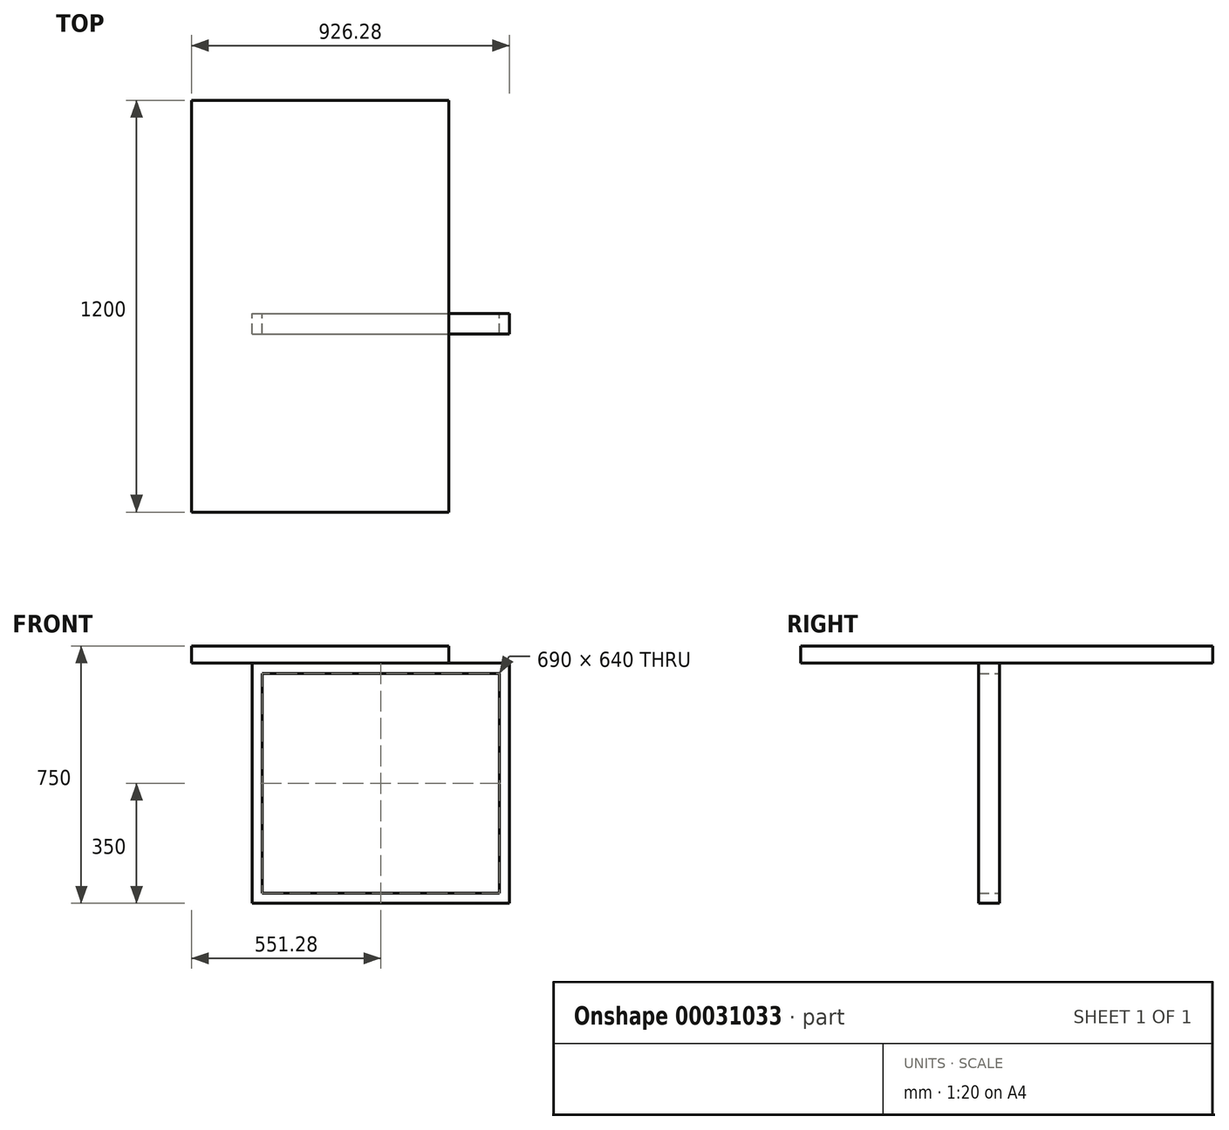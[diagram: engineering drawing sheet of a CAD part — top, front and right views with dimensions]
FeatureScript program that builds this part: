
annotation { "Feature Type Name" : "Feature", "Feature Type Description" : "" }
export const myFeature = defineFeature(function(context is Context, id is Id, definition is map)
    precondition{}
    {
        {
            var Q0;
            Q0=qCreatedBy(makeId("Front.planeOp"),FACE);
            var sketch = newSketch(context, id + "F0", { "sketchPlane" : qUnion([Q0])});
            skLineSegment(sketch, "E0.top", {"start": v(-375, -700) * mm, "end": v(375, -700) * mm});
            skLineSegment(sketch, "E0.left", {"start": v(-375, 0) * mm, "end": v(-375, -700) * mm});
            skLineSegment(sketch, "E0.right", {"start": v(375, 0) * mm, "end": v(375, -700) * mm});
            skLineSegment(sketch, "E1.0", {"start": v(-345, -670) * mm, "end": v(345, -670) * mm});
            skLineSegment(sketch, "E1.1", {"start": v(-345, -30) * mm, "end": v(-345, -670) * mm});
            skLineSegment(sketch, "E1.2", {"start": v(-345, -30) * mm, "end": v(345, -30) * mm});
            skLineSegment(sketch, "E1.3", {"start": v(345, -30) * mm, "end": v(345, -670) * mm});
            skLineSegment(sketch, "E2", {"start": v(0, 0) * mm, "end": v(0, -814.9) * mm, "construction": true});
            skLineSegment(sketch, "E3", {"start": v(-375, 0) * mm, "end": v(375, 0) * mm});
            skSolve(sketch);
        }
        {
            var Q0;
            Q0 = qSketchRegion(id + "F0", true);
            extrude(context, id + "F1", {"entities" : qUnion([Q0]), "depth" : 60 * mm});
        }
        {
            var Q0;
            Q0=qCreatedBy(makeId("Top.planeOp"),FACE);
            var sketch = newSketch(context, id + "F2", { "sketchPlane" : qUnion([Q0])});
            skLineSegment(sketch, "E4.bottom", {"start": v(-551.28, 620.86) * mm, "end": v(198.72, 620.86) * mm});
            skLineSegment(sketch, "E4.top", {"start": v(-551.28, -579.14) * mm, "end": v(198.72, -579.14) * mm});
            skLineSegment(sketch, "E4.left", {"start": v(-551.28, 620.86) * mm, "end": v(-551.28, -579.14) * mm});
            skLineSegment(sketch, "E4.right", {"start": v(198.72, 620.86) * mm, "end": v(198.72, -579.14) * mm});
            skSolve(sketch);
        }
        {
            var Q0;
            Q0 = qSketchRegion(id + "F2", true);
            extrude(context, id + "F3", {"entities" : qUnion([Q0]), "depth" : 50 * mm});
        }
    });
